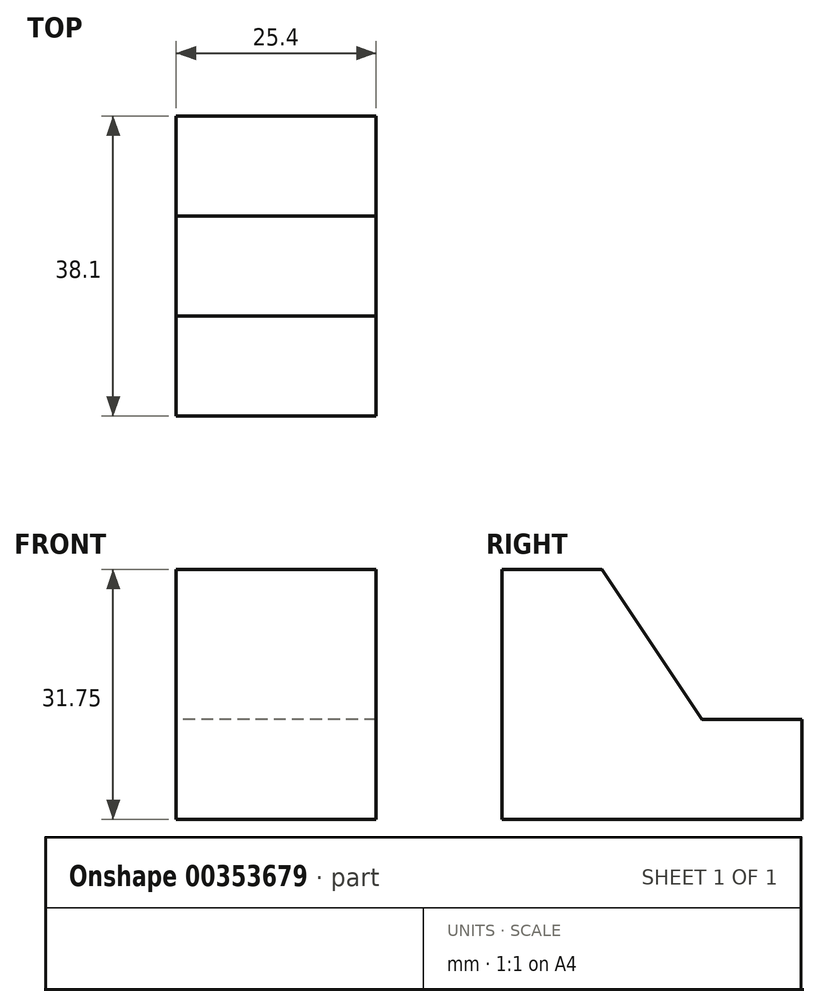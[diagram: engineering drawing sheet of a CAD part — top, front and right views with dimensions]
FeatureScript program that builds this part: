
annotation { "Feature Type Name" : "Feature", "Feature Type Description" : "" }
export const myFeature = defineFeature(function(context is Context, id is Id, definition is map)
    precondition{}
    {
        {
            var Q0;
            Q0=qCreatedBy(makeId("Right.planeOp"),FACE);
            var sketch = newSketch(context, id + "F0", { "sketchPlane" : qUnion([Q0])});
            skLineSegment(sketch, "E0", {"start": v(-35.98, 31.75) * mm, "end": v(-48.68, 31.75) * mm});
            skLineSegment(sketch, "E1", {"start": v(-48.68, 31.75) * mm, "end": v(-48.68, 0) * mm});
            skLineSegment(sketch, "E2", {"start": v(-48.68, 0) * mm, "end": v(-10.58, 0) * mm});
            skLineSegment(sketch, "E3", {"start": v(-10.58, 0) * mm, "end": v(-10.58, 12.7) * mm});
            skLineSegment(sketch, "E4", {"start": v(-10.58, 12.7) * mm, "end": v(-23.28, 12.7) * mm});
            skLineSegment(sketch, "E5", {"start": v(-23.28, 12.7) * mm, "end": v(-35.98, 31.75) * mm});
            skSolve(sketch);
        }
        {
            var Q0;
            Q0=makeQuery(id+"F0.imprint","IMPRINT",FACE,{"disambiguationData":[TD([[makeQuery(id+"F0.imprint","IMPRINT",EDGE,{"derivedFrom":sQuery(id+"F0.wireOp",EDGE,"E0")}),1.0]])]});
            extrude(context, id + "F1", {"entities" : qUnion([Q0]), "depth" : 25.4 * mm});
        }
    });
